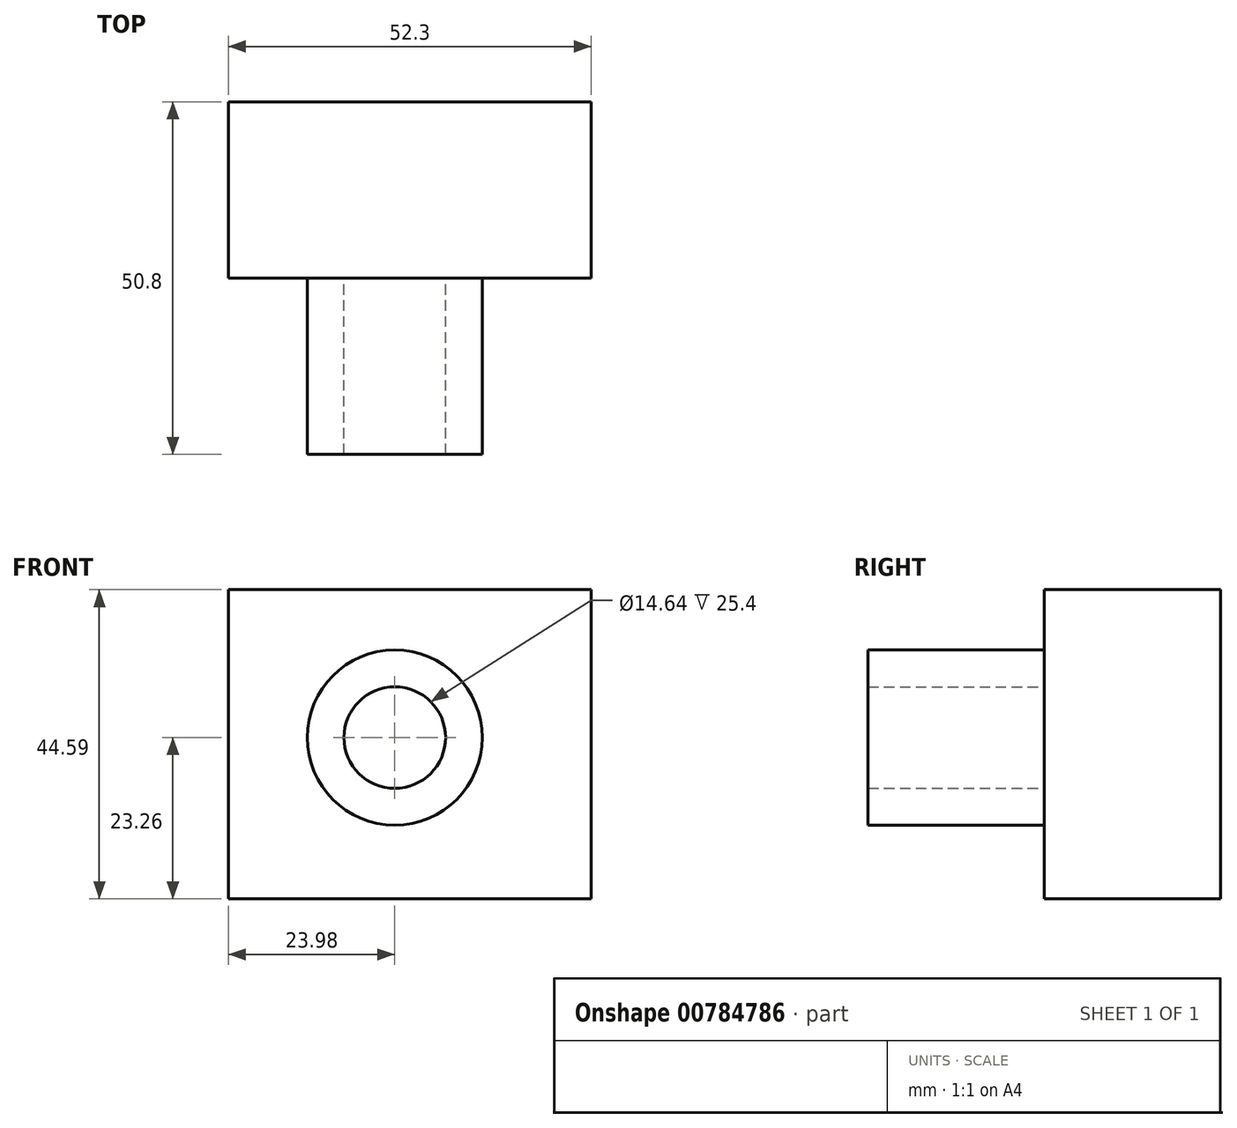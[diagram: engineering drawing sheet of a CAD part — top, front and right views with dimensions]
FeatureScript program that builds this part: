
annotation { "Feature Type Name" : "Feature", "Feature Type Description" : "" }
export const myFeature = defineFeature(function(context is Context, id is Id, definition is map)
    precondition{}
    {
        {
            var Q0;
            Q0=qCreatedBy(makeId("Front.planeOp"),FACE);
            var sketch = newSketch(context, id + "F0", { "sketchPlane" : qUnion([Q0])});
            skLineSegment(sketch, "E0.bottom", {"start": v(-41.09, 31.45) * mm, "end": v(44.22, 31.45) * mm});
            skLineSegment(sketch, "E0.top", {"start": v(-41.09, -35.3) * mm, "end": v(44.22, -35.3) * mm});
            skLineSegment(sketch, "E0.left", {"start": v(-41.09, 31.45) * mm, "end": v(-41.09, -35.3) * mm});
            skLineSegment(sketch, "E0.right", {"start": v(44.22, 31.45) * mm, "end": v(44.22, -35.3) * mm});
            skCircle(sketch, "E1", {"center": v(0, 0) * mm, "radius": 7.32 * mm});
            skCircle(sketch, "E2", {"center": v(0, 0) * mm, "radius": 12.62 * mm});
            skSolve(sketch);
        }
        {
            var Q0;
            Q0=makeQuery(id+"F0.imprint","IMPRINT",FACE,{"disambiguationData":[TD([[makeQuery(id+"F0.imprint","IMPRINT",EDGE,{"derivedFrom":sQuery(id+"F0.wireOp",EDGE,"E1")}),-1.0]])]});
            extrude(context, id + "F1", {"entities" : qUnion([Q0]), "depth" : 50.8 * mm, "offsetDistance" : 25.4 * mm});
        }
        {
            var Q0;
            Q0=qCreatedBy(makeId("Front.planeOp"),FACE);
            var sketch = newSketch(context, id + "F2", { "sketchPlane" : qUnion([Q0])});
            skLineSegment(sketch, "E3.bottom", {"start": v(-23.98, 21.33) * mm, "end": v(28.32, 21.33) * mm});
            skLineSegment(sketch, "E3.top", {"start": v(-23.98, -23.26) * mm, "end": v(28.32, -23.26) * mm});
            skLineSegment(sketch, "E3.left", {"start": v(-23.98, 21.33) * mm, "end": v(-23.98, -23.26) * mm});
            skLineSegment(sketch, "E3.right", {"start": v(28.32, 21.33) * mm, "end": v(28.32, -23.26) * mm});
            skSolve(sketch);
        }
        {
            var Q0;
            Q0=makeQuery(id+"F2.imprint","IMPRINT",FACE,{"disambiguationData":[TD([[makeQuery(id+"F2.imprint","IMPRINT",EDGE,{"derivedFrom":sQuery(id+"F2.wireOp",EDGE,"E3.bottom")}),-1.0]])]});
            extrude(context, id + "F3", {"entities" : qUnion([Q0]), "operationType" : NewBodyOperationType.ADD, "depth" : 25.4 * mm, "offsetDistance" : 25.4 * mm});
        }
    });
